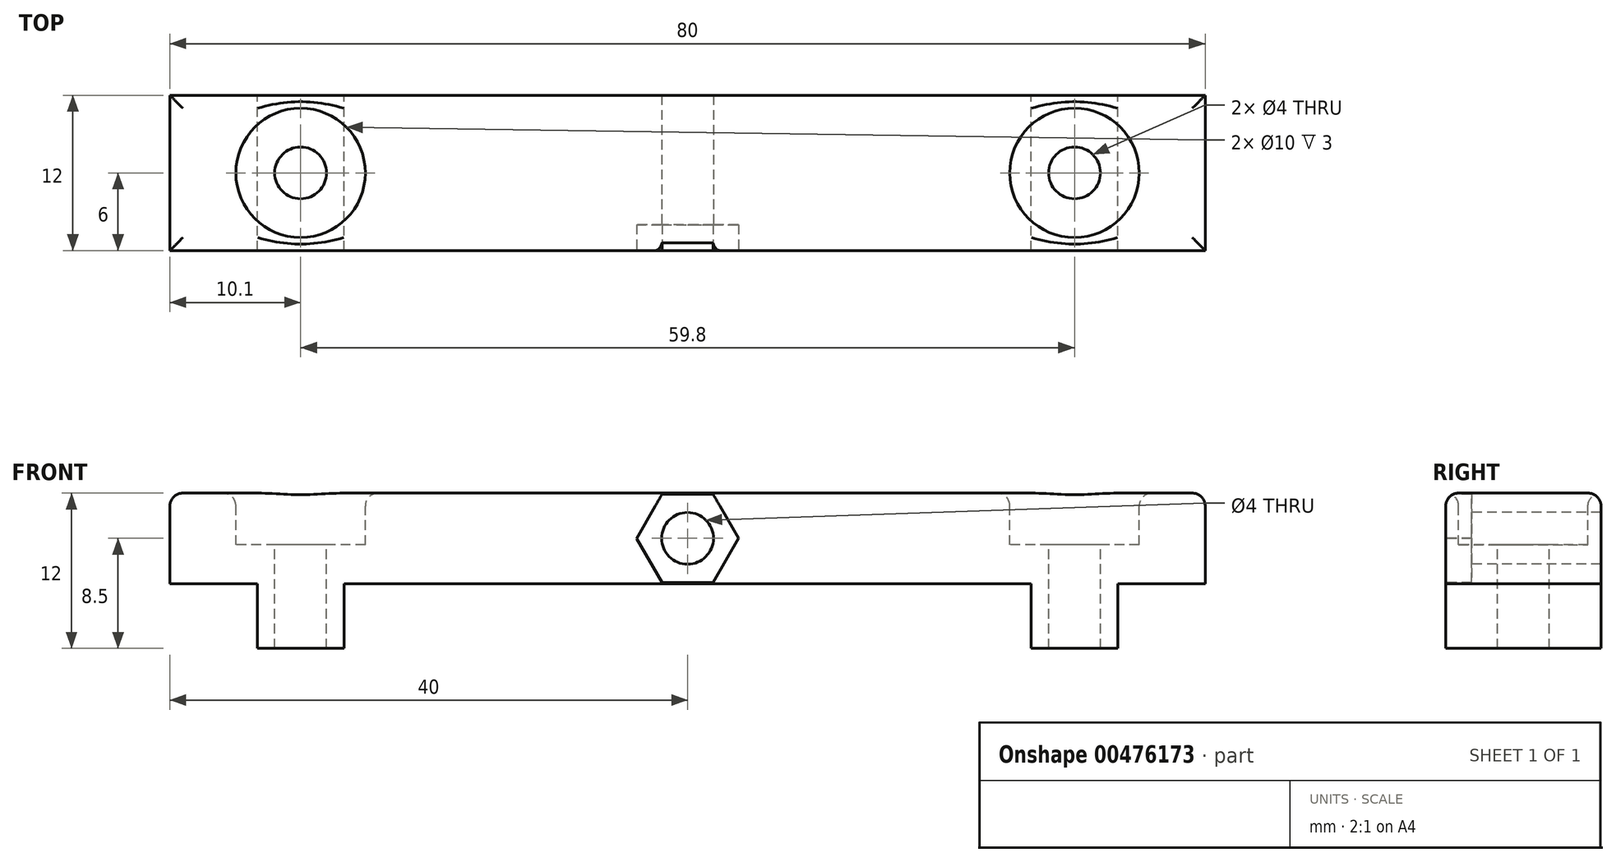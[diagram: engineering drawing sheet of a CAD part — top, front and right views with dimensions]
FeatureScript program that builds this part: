
annotation { "Feature Type Name" : "Feature", "Feature Type Description" : "" }
export const myFeature = defineFeature(function(context is Context, id is Id, definition is map)
    precondition{}
    {
        {
            var Q0;
            Q0=qCreatedBy(makeId("Front.planeOp"),FACE);
            var sketch = newSketch(context, id + "F0", { "sketchPlane" : qUnion([Q0])});
            skLineSegment(sketch, "E0.bottom", {"start": v(6.75, 0) * mm, "end": v(13.45, 0) * mm});
            skLineSegment(sketch, "E0.top", {"start": v(0, 12) * mm, "end": v(80, 12) * mm});
            skLineSegment(sketch, "E0.left", {"start": v(0, 5) * mm, "end": v(0, 12) * mm});
            skLineSegment(sketch, "E0.right", {"start": v(80, 5) * mm, "end": v(80, 12) * mm});
            skLineSegment(sketch, "E1", {"start": v(6.75, 5) * mm, "end": v(6.75, 0) * mm});
            skLineSegment(sketch, "E2", {"start": v(13.45, 5) * mm, "end": v(13.45, 0) * mm});
            skLineSegment(sketch, "E3", {"start": v(66.55, 5) * mm, "end": v(66.55, 0) * mm});
            skLineSegment(sketch, "E4", {"start": v(73.25, 5) * mm, "end": v(73.25, 0) * mm});
            skLineSegment(sketch, "E5", {"start": v(0, 5) * mm, "end": v(80, 5) * mm});
            skLineSegment(sketch, "E6.trimOffspring", {"start": v(66.55, 0) * mm, "end": v(73.25, 0) * mm});
            skLineSegment(sketch, "E7", {"start": v(10.1, 0) * mm, "end": v(10.1, 12) * mm});
            skLineSegment(sketch, "E8", {"start": v(69.9, 0) * mm, "end": v(69.9, 12) * mm});
            skSolve(sketch);
        }
        {
            var Q0;
            Q0 = qSketchRegion(id + "F0", true);
            extrude(context, id + "F1", {"entities" : qUnion([Q0]), "depth" : 12 * mm});
        }
        {
            var Q0;
            Q0=makeQuery(id+"F1.opExtrude","SWEPT_FACE",FACE,{"disambiguationData":[OSD([sQuery(id+"F0.wireOp",EDGE,"E0.top")])]});
            var sketch = newSketch(context, id + "F2", { "sketchPlane" : qUnion([Q0])});
            skLineSegment(sketch, "E9", {"start": v(0, -6) * mm, "end": v(80, -6) * mm});
            skLineSegment(sketch, "E10", {"start": v(10.1, 0) * mm, "end": v(10.1, -12) * mm});
            skLineSegment(sketch, "E11", {"start": v(69.9, 0) * mm, "end": v(69.9, -12) * mm});
            skCircle(sketch, "E12", {"center": v(10.1, -6) * mm, "radius": 0.7 * mm});
            skCircle(sketch, "E13", {"center": v(69.9, -6) * mm, "radius": 1.06 * mm});
            skSolve(sketch);
        }
        {
            var Q0;
            Q0=sQuery(id+"F2.wireOp",VERTEX,"E12.center");
            var Q1;
            Q1=sQuery(id+"F2.wireOp",VERTEX,"E13.center");
            var Q2;
            Q2=makeQuery(id+"F1.opExtrude","SWEPT_BODY",BODY,{"disambiguationData":[OSD([sQuery(id+"F0.wireOp",EDGE,"E0.bottom"),sQuery(id+"F0.wireOp",EDGE,"E0.top"),sQuery(id+"F0.wireOp",EDGE,"E0.left"),sQuery(id+"F0.wireOp",EDGE,"E0.right"),sQuery(id+"F0.wireOp",EDGE,"E1"),sQuery(id+"F0.wireOp",EDGE,"E2"),sQuery(id+"F0.wireOp",EDGE,"E3"),sQuery(id+"F0.wireOp",EDGE,"E4"),sQuery(id+"F0.wireOp",EDGE,"E5"),sQuery(id+"F0.wireOp",EDGE,"E6.trimOffspring")])]});
            hole(context, id + "F3", {"style" : HoleStyle.C_BORE, "endStyle" : HoleEndStyle.BLIND, "holeDiameter" : 4 * mm, "cBoreDiameter" : 10 * mm, "cBoreDepth" : 4 * mm, "holeDepth" : 25 * mm, "isTappedThrough" : true, "tappedDepth" : 12 * mm, "tapClearance" : 3, "startFromSketch" : true, "locations" : qUnion([Q0, Q1]), "scope" : qUnion([Q2])});
        }
        {
            var Q0;
            Q0=makeQuery(id+"F1.opExtrude","CAP_FACE",FACE,{"disambiguationData":[OSD([sQuery(id+"F0.wireOp",EDGE,"E0.bottom"),sQuery(id+"F0.wireOp",EDGE,"E0.top"),sQuery(id+"F0.wireOp",EDGE,"E0.left"),sQuery(id+"F0.wireOp",EDGE,"E0.right"),sQuery(id+"F0.wireOp",EDGE,"E1"),sQuery(id+"F0.wireOp",EDGE,"E2"),sQuery(id+"F0.wireOp",EDGE,"E3"),sQuery(id+"F0.wireOp",EDGE,"E4"),sQuery(id+"F0.wireOp",EDGE,"E5"),sQuery(id+"F0.wireOp",EDGE,"E6.trimOffspring")])],"isStart":false});
            var sketch = newSketch(context, id + "F4", { "sketchPlane" : qUnion([Q0])});
            skLineSegment(sketch, "E14", {"start": v(0, 8.5) * mm, "end": v(80, 8.5) * mm});
            skLineSegment(sketch, "E15", {"start": v(40, 12) * mm, "end": v(40, 5) * mm});
            skCircle(sketch, "E16", {"center": v(40, 8.5) * mm, "radius": 1.42 * mm});
            skCircle(sketch, "E17.cCircle", {"center": v(40, 8.5) * mm, "radius": 3.42 * mm, "construction": true});
            skLineSegment(sketch, "E17.0", {"start": v(43.94, 8.5) * mm, "end": v(41.97, 5.09) * mm});
            skLineSegment(sketch, "E17.1", {"start": v(41.97, 5.09) * mm, "end": v(38.03, 5.08) * mm});
            skLineSegment(sketch, "E17.2", {"start": v(38.03, 5.08) * mm, "end": v(36.06, 8.5) * mm});
            skLineSegment(sketch, "E17.3", {"start": v(36.06, 8.5) * mm, "end": v(38.03, 11.91) * mm});
            skLineSegment(sketch, "E17.4", {"start": v(38.03, 11.91) * mm, "end": v(41.97, 11.92) * mm});
            skLineSegment(sketch, "E17.5", {"start": v(41.97, 11.92) * mm, "end": v(43.94, 8.5) * mm});
            skPoint(sketch, "E17.0.midPoint", {"position": v(42.96, 6.8) * mm});
            skSolve(sketch);
        }
        {
            var Q0;
            Q0=sQuery(id+"F4.wireOp",VERTEX,"E16.center");
            var Q1;
            Q1=makeQuery(id+"F1.opExtrude","SWEPT_BODY",BODY,{"disambiguationData":[OSD([sQuery(id+"F0.wireOp",EDGE,"E0.bottom"),sQuery(id+"F0.wireOp",EDGE,"E0.top"),sQuery(id+"F0.wireOp",EDGE,"E0.left"),sQuery(id+"F0.wireOp",EDGE,"E0.right"),sQuery(id+"F0.wireOp",EDGE,"E1"),sQuery(id+"F0.wireOp",EDGE,"E2"),sQuery(id+"F0.wireOp",EDGE,"E3"),sQuery(id+"F0.wireOp",EDGE,"E4"),sQuery(id+"F0.wireOp",EDGE,"E5"),sQuery(id+"F0.wireOp",EDGE,"E6.trimOffspring")])]});
            hole(context, id + "F5", {"style" : HoleStyle.SIMPLE, "endStyle" : HoleEndStyle.BLIND, "holeDiameter" : 4 * mm, "holeDepth" : 25 * mm, "isTappedThrough" : true, "tappedDepth" : 12 * mm, "tapClearance" : 3, "startFromSketch" : true, "locations" : qUnion([Q0]), "scope" : qUnion([Q1])});
        }
        {
            var Q0;
            Q0 = qSketchRegion(id + "F4", true);
            extrude(context, id + "F6", {"entities" : qUnion([Q0]), "operationType" : NewBodyOperationType.REMOVE, "oppositeDirection" : true, "depth" : 2 * mm});
        }
        {
            var Q0;
            Q0=makeQuery(id+"F1.opExtrude","SWEPT_FACE",FACE,{"disambiguationData":[OSD([sQuery(id+"F0.wireOp",EDGE,"E0.top")])]});
            fillet(context, id + "F7", {"entities" : qUnion([Q0]), "radius" : 1 * mm, "tangentPropagation" : true, "allowEdgeOverflow" : false});
        }
    });
